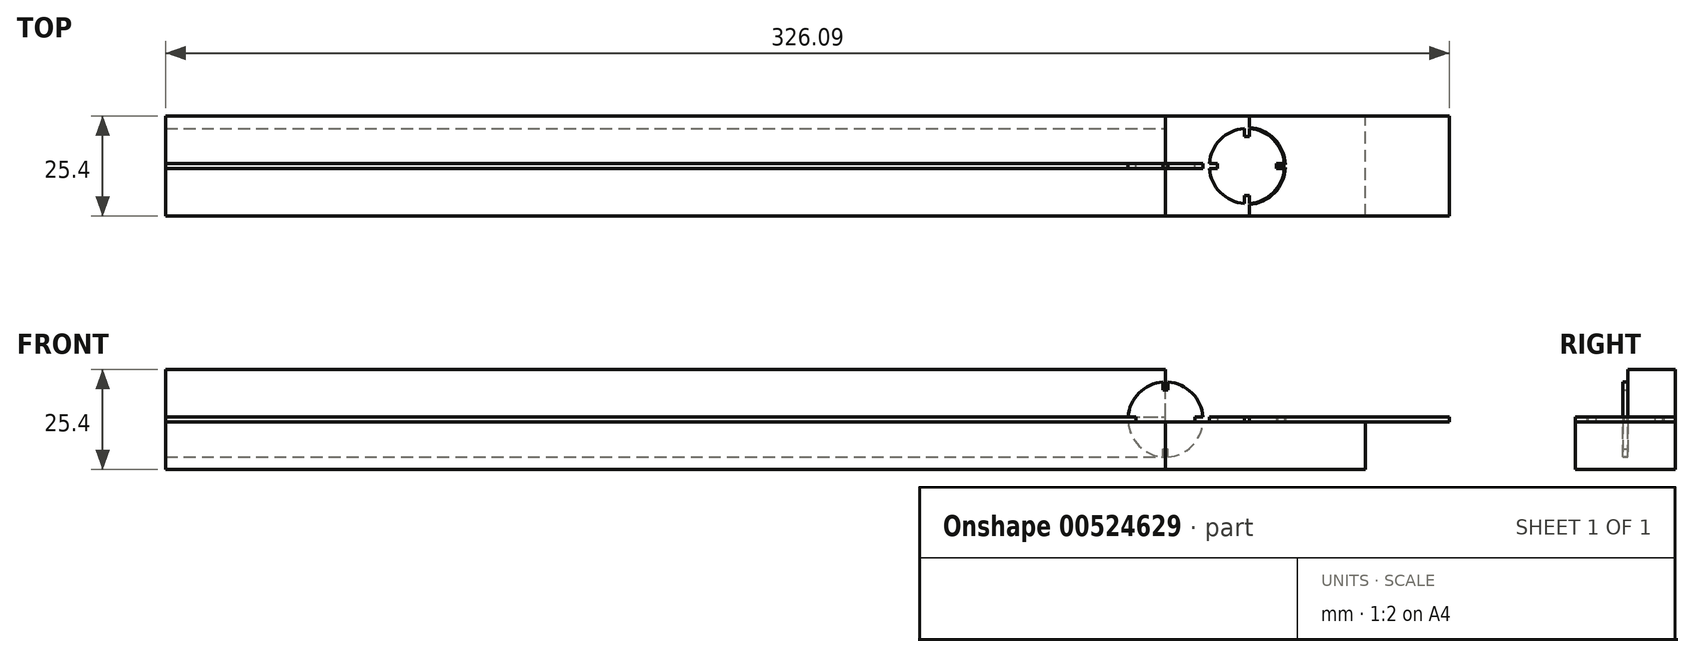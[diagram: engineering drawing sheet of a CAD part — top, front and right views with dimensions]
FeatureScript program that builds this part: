
annotation { "Feature Type Name" : "Feature", "Feature Type Description" : "" }
export const myFeature = defineFeature(function(context is Context, id is Id, definition is map)
    precondition{}
    {
        {
            var Q0;
            Q0=qCreatedBy(makeId("Front.planeOp"),FACE);
            var sketch = newSketch(context, id + "F0", { "sketchPlane" : qUnion([Q0])});
            skArc(sketch, "E0", {"start": v(-0.64, 9.5) * mm, "mid": v(-6.74, 6.74) * mm, "end": v(-9.5, 0.63) * mm});
            skLineSegment(sketch, "E1.top", {"start": v(-0.64, 7.47) * mm, "end": v(0.64, 7.47) * mm});
            skLineSegment(sketch, "E1.left", {"start": v(-0.64, 9.5) * mm, "end": v(-0.64, 7.47) * mm});
            skLineSegment(sketch, "E1.right", {"start": v(0.64, 9.5) * mm, "end": v(0.64, 7.47) * mm});
            skLineSegment(sketch, "E2.bottom", {"start": v(-9.5, 0.64) * mm, "end": v(-7.47, 0.64) * mm});
            skLineSegment(sketch, "E2.top", {"start": v(-9.5, -0.64) * mm, "end": v(-7.47, -0.64) * mm});
            skLineSegment(sketch, "E2.right", {"start": v(-7.47, 0.64) * mm, "end": v(-7.47, -0.64) * mm});
            skLineSegment(sketch, "E3.MirrorCS", {"start": v(-0.64, -7.47) * mm, "end": v(0.64, -7.47) * mm});
            skLineSegment(sketch, "E4.MirrorCS", {"start": v(0.64, -9.5) * mm, "end": v(0.64, -7.47) * mm});
            skLineSegment(sketch, "E5.MirrorCS", {"start": v(-0.64, -9.5) * mm, "end": v(-0.64, -7.47) * mm});
            skLineSegment(sketch, "E6.MirrorCS", {"start": v(7.47, 0.64) * mm, "end": v(7.47, -0.64) * mm});
            skLineSegment(sketch, "E7.MirrorCS", {"start": v(9.5, 0.64) * mm, "end": v(7.47, 0.64) * mm});
            skLineSegment(sketch, "E8.MirrorCS", {"start": v(9.5, -0.64) * mm, "end": v(7.47, -0.64) * mm});
            skArc(sketch, "E9.trimOffspring", {"start": v(9.5, 0.64) * mm, "mid": v(6.74, 6.74) * mm, "end": v(0.64, 9.5) * mm});
            skArc(sketch, "E10.trimOffspring", {"start": v(0.63, -9.5) * mm, "mid": v(6.74, -6.74) * mm, "end": v(9.5, -0.64) * mm});
            skArc(sketch, "E11.trimOffspring", {"start": v(-9.5, -0.64) * mm, "mid": v(-6.74, -6.74) * mm, "end": v(-0.64, -9.5) * mm});
            skSolve(sketch);
        }
        {
            var Q0;
            Q0=makeQuery(id+"F0.imprint","IMPRINT",FACE,{"disambiguationData":[TD([[makeQuery(id+"F0.imprint","IMPRINT",EDGE,{"derivedFrom":sQuery(id+"F0.wireOp",EDGE,"E0")}),1.0]])]});
            extrude(context, id + "F1", {"entities" : qUnion([Q0]), "endBound" : BoundingType.SYMMETRIC, "depth" : 1.27 * mm, "offsetDistance" : 25.4 * mm});
        }
        {
            var Q0;
            Q0=qCreatedBy(makeId("Top.planeOp"),FACE);
            var sketch = newSketch(context, id + "F2", { "sketchPlane" : qUnion([Q0])});
            skArc(sketch, "E12", {"start": v(21.3, -9.5) * mm, "mid": v(27.4, -6.74) * mm, "end": v(30.16, -0.64) * mm});
            skLineSegment(sketch, "E13.bottom", {"start": v(11.16, 0.64) * mm, "end": v(13.19, 0.64) * mm});
            skLineSegment(sketch, "E13.top", {"start": v(11.16, -0.64) * mm, "end": v(13.19, -0.64) * mm});
            skLineSegment(sketch, "E13.right", {"start": v(13.19, 0.64) * mm, "end": v(13.19, -0.64) * mm});
            skLineSegment(sketch, "E14.bottom", {"start": v(28.13, 0.64) * mm, "end": v(30.16, 0.64) * mm});
            skLineSegment(sketch, "E14.top", {"start": v(28.13, -0.64) * mm, "end": v(30.16, -0.64) * mm});
            skLineSegment(sketch, "E14.left", {"start": v(28.13, 0.63) * mm, "end": v(28.13, -0.64) * mm});
            skLineSegment(sketch, "E15.bottom", {"start": v(20.03, 7.47) * mm, "end": v(20.03, 9.5) * mm});
            skLineSegment(sketch, "E15.top", {"start": v(21.3, 7.47) * mm, "end": v(21.3, 9.5) * mm});
            skLineSegment(sketch, "E15.left", {"start": v(20.03, 7.47) * mm, "end": v(21.3, 7.47) * mm});
            skLineSegment(sketch, "E16.bottom", {"start": v(21.3, -7.47) * mm, "end": v(21.3, -9.5) * mm});
            skLineSegment(sketch, "E16.top", {"start": v(20.03, -7.47) * mm, "end": v(20.03, -9.5) * mm});
            skLineSegment(sketch, "E16.left", {"start": v(21.3, -7.47) * mm, "end": v(20.03, -7.47) * mm});
            skArc(sketch, "E17.trimOffspring", {"start": v(11.16, -0.64) * mm, "mid": v(13.93, -6.74) * mm, "end": v(20.03, -9.5) * mm});
            skArc(sketch, "E18.trimOffspring", {"start": v(30.16, 0.64) * mm, "mid": v(27.4, 6.74) * mm, "end": v(21.3, 9.5) * mm});
            skArc(sketch, "E19.trimOffspring", {"start": v(20.03, 9.5) * mm, "mid": v(13.93, 6.74) * mm, "end": v(11.16, 0.64) * mm});
            skSolve(sketch);
        }
        {
            var Q0;
            Q0=makeQuery(id+"F2.imprint","IMPRINT",FACE,{"disambiguationData":[TD([[makeQuery(id+"F2.imprint","IMPRINT",EDGE,{"derivedFrom":sQuery(id+"F2.wireOp",EDGE,"E12")}),1.0]])]});
            extrude(context, id + "F3", {"entities" : qUnion([Q0]), "endBound" : BoundingType.SYMMETRIC, "depth" : 1.27 * mm, "offsetDistance" : 25.4 * mm});
        }
        {
            var Q0;
            Q0=qCreatedBy(makeId("Right.planeOp"),FACE);
            var sketch = newSketch(context, id + "F4", { "sketchPlane" : qUnion([Q0])});
            skLineSegment(sketch, "E20.bottom", {"start": v(12.7, -12.7) * mm, "end": v(-12.7, -12.7) * mm});
            skLineSegment(sketch, "E20.top", {"start": v(12.7, 12.7) * mm, "end": v(0.66, 12.7) * mm});
            skLineSegment(sketch, "E20.left", {"start": v(12.7, -12.7) * mm, "end": v(12.7, 12.7) * mm});
            skLineSegment(sketch, "E20.right", {"start": v(-12.7, -12.7) * mm, "end": v(-12.7, -0.66) * mm});
            skPoint(sketch, "E20.middle", {"position": v(0, 0) * mm});
            skLineSegment(sketch, "E21.bottom", {"start": v(0.66, -9.55) * mm, "end": v(-0.66, -9.55) * mm});
            skLineSegment(sketch, "E21.left", {"start": v(0.66, -9.55) * mm, "end": v(0.66, -0.66) * mm});
            skLineSegment(sketch, "E21.right", {"start": v(-0.66, -9.55) * mm, "end": v(-0.66, -0.66) * mm});
            skLineSegment(sketch, "E22.bottom", {"start": v(9.55, -0.66) * mm, "end": v(0.66, -0.66) * mm});
            skLineSegment(sketch, "E22.top", {"start": v(9.55, 0.66) * mm, "end": v(0.66, 0.66) * mm});
            skLineSegment(sketch, "E22.left", {"start": v(9.55, -0.66) * mm, "end": v(9.55, 0.66) * mm});
            skLineSegment(sketch, "E23", {"start": v(0.66, 9.55) * mm, "end": v(0.66, 12.7) * mm});
            skLineSegment(sketch, "E24", {"start": v(-9.55, -0.66) * mm, "end": v(-12.7, -0.66) * mm});
            skLineSegment(sketch, "E25.trimOffspring", {"start": v(0.66, 0.66) * mm, "end": v(0.66, 9.55) * mm});
            skLineSegment(sketch, "E26.trimOffspring", {"start": v(-0.66, -0.66) * mm, "end": v(-9.55, -0.66) * mm});
            skSolve(sketch);
        }
        {
            var Q0;
            Q0=makeQuery(id+"F4.imprint","IMPRINT",FACE,{"disambiguationData":[TD([[makeQuery(id+"F4.imprint","IMPRINT",EDGE,{"derivedFrom":sQuery(id+"F4.wireOp",EDGE,"E20.bottom")}),-1.0]])]});
            extrude(context, id + "F5", {"entities" : qUnion([Q0]), "oppositeDirection" : true, "depth" : 254 * mm, "offsetDistance" : 25.4 * mm});
        }
        {
            var Q0;
            Q0=makeQuery(id+"F5.opExtrude","CAP_FACE",FACE,{"disambiguationData":[OSD([sQuery(id+"F4.wireOp",EDGE,"E20.bottom"),sQuery(id+"F4.wireOp",EDGE,"E20.top"),sQuery(id+"F4.wireOp",EDGE,"E20.left"),sQuery(id+"F4.wireOp",EDGE,"E20.right"),sQuery(id+"F4.wireOp",EDGE,"E21.bottom"),sQuery(id+"F4.wireOp",EDGE,"E21.left"),sQuery(id+"F4.wireOp",EDGE,"E21.right"),sQuery(id+"F4.wireOp",EDGE,"E22.bottom"),sQuery(id+"F4.wireOp",EDGE,"E22.top"),sQuery(id+"F4.wireOp",EDGE,"E22.left"),sQuery(id+"F4.wireOp",EDGE,"E23"),sQuery(id+"F4.wireOp",EDGE,"E24"),sQuery(id+"F4.wireOp",EDGE,"E25.trimOffspring"),sQuery(id+"F4.wireOp",EDGE,"E26.trimOffspring")])],"isStart":true});
            var sketch = newSketch(context, id + "F6", { "sketchPlane" : qUnion([Q0])});
            skLineSegment(sketch, "E27.bottom", {"start": v(-12.7, -0.66) * mm, "end": v(12.7, -0.66) * mm});
            skLineSegment(sketch, "E27.top", {"start": v(-12.7, -12.7) * mm, "end": v(12.7, -12.7) * mm});
            skLineSegment(sketch, "E27.left", {"start": v(-12.7, -0.66) * mm, "end": v(-12.7, -12.7) * mm});
            skLineSegment(sketch, "E27.right", {"start": v(12.7, -0.66) * mm, "end": v(12.7, -12.7) * mm});
            skSolve(sketch);
        }
        {
            var Q0;
            Q0 = qSketchRegion(id + "F6", true);
            extrude(context, id + "F7", {"entities" : qUnion([Q0]), "depth" : 50.8 * mm, "offsetDistance" : 25.4 * mm});
        }
        {
            var Q0;
            Q0=qCreatedBy(makeId("Top.planeOp"),FACE);
            var sketch = newSketch(context, id + "F8", { "sketchPlane" : qUnion([Q0])});
            skLineSegment(sketch, "E28.bottom", {"start": v(21.3, -12.7) * mm, "end": v(72.1, -12.7) * mm});
            skLineSegment(sketch, "E28.top", {"start": v(21.3, 12.7) * mm, "end": v(72.1, 12.7) * mm});
            skLineSegment(sketch, "E28.left", {"start": v(21.3, -12.7) * mm, "end": v(21.3, 12.7) * mm});
            skLineSegment(sketch, "E28.right", {"start": v(72.1, -12.7) * mm, "end": v(72.1, 12.7) * mm});
            skPoint(sketch, "E28.middle", {"position": v(46.7, 0) * mm});
            skSolve(sketch);
        }
        {
            var Q0;
            Q0 = qSketchRegion(id + "F8", true);
            extrude(context, id + "F9", {"entities" : qUnion([Q0]), "endBound" : BoundingType.SYMMETRIC, "depth" : 1.27 * mm, "offsetDistance" : 25.4 * mm});
        }
        {
            var Q0;
            Q0=makeQuery(id+"F3.opExtrude","SWEPT_BODY",BODY,{"disambiguationData":[OSD([sQuery(id+"F2.wireOp",EDGE,"E12"),sQuery(id+"F2.wireOp",EDGE,"E13.bottom"),sQuery(id+"F2.wireOp",EDGE,"E13.top"),sQuery(id+"F2.wireOp",EDGE,"E13.right"),sQuery(id+"F2.wireOp",EDGE,"E14.bottom"),sQuery(id+"F2.wireOp",EDGE,"E14.top"),sQuery(id+"F2.wireOp",EDGE,"E14.left"),sQuery(id+"F2.wireOp",EDGE,"E15.bottom"),sQuery(id+"F2.wireOp",EDGE,"E15.top"),sQuery(id+"F2.wireOp",EDGE,"E15.left"),sQuery(id+"F2.wireOp",EDGE,"E16.bottom"),sQuery(id+"F2.wireOp",EDGE,"E16.top"),sQuery(id+"F2.wireOp",EDGE,"E16.left"),sQuery(id+"F2.wireOp",EDGE,"E17.trimOffspring"),sQuery(id+"F2.wireOp",EDGE,"E18.trimOffspring"),sQuery(id+"F2.wireOp",EDGE,"E19.trimOffspring")])]});
            var Q1;
            Q1=makeQuery(id+"F9.opExtrude","SWEPT_BODY",BODY,{"disambiguationData":[OSD([sQuery(id+"F8.wireOp",EDGE,"E28.bottom"),sQuery(id+"F8.wireOp",EDGE,"E28.top"),sQuery(id+"F8.wireOp",EDGE,"E28.left"),sQuery(id+"F8.wireOp",EDGE,"E28.right")])]});
            booleanBodies(context, id + "F10", {"operationType" : BooleanOperationType.SUBTRACTION, "tools" : qUnion([Q0]), "targets" : qUnion([Q1]), "offset" : true, "offsetAll" : true, "offsetDistance" : 0.25 * mm, "keepTools" : true});
        }
    });
